# Revit family: FireFighting_Hydrant-Pipe-Riser-Kit_Galvin_100TEx1600
name_source: partatom
category: Mechanical Equipment
revit_build: Autodesk Revit MEP 2012 (Build: 20110916_2132(x64)
units: mm (PartAtom-declared; Revit-internal decimal feet)

## types (1)
- 381332
    Assembly Code = D4030
    Description = Hydrant Pipe Riser Kit with Roll Groove T-Head & Qld Valves & Caps 100TD x 1600 (Galv & Painted)
    DimDepth = 215 mm
    DimHeight = 1182 mm  [stored 3.87795 ft]
    DimWidth = 668 mm  [stored 2.1916 ft]
    FilterObject_ANZRS = 381332
    FlowRate = 0.00 L/s
    Instructions = http://www.galvinengineering.com.au
    Keynote = 10520
    Manufacturer = Galvin Engineering
    Model = 381332
    ModifiedIssue_ANZRS = 20140330 $
    StyleOrType_ANZRS = Fire Fighting Equipment
    Type Comments = 381332
    URL = www.galvinengineering.com.au

note: [stored X ft] marks values corroborated as IEEE doubles in the binary element streams (Revit-internal decimal feet)

## geometry (parser evidence)
native form markers: Sweep x1
no freeform markers — native parametric forms only
